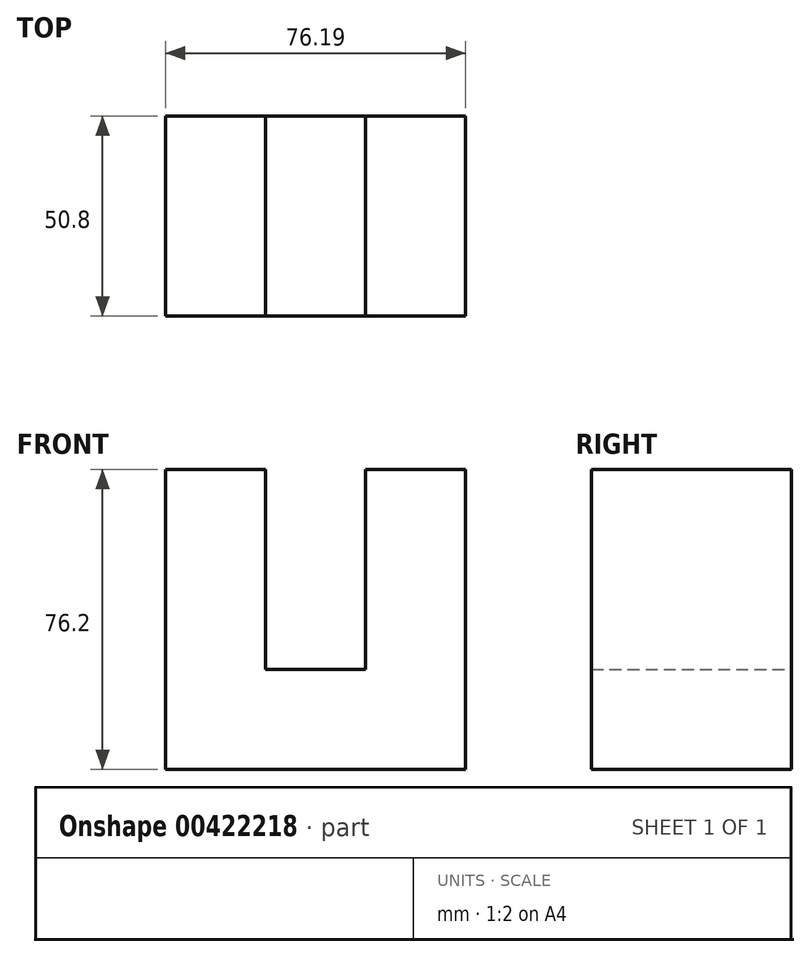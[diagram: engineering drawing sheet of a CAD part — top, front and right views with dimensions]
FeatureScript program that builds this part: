
annotation { "Feature Type Name" : "Feature", "Feature Type Description" : "" }
export const myFeature = defineFeature(function(context is Context, id is Id, definition is map)
    precondition{}
    {
        {
            var Q0;
            Q0=qCreatedBy(makeId("Front.planeOp"),FACE);
            var sketch = newSketch(context, id + "F0", { "sketchPlane" : qUnion([Q0])});
            skLineSegment(sketch, "E0", {"start": v(0, 0) * mm, "end": v(-76.2, 0) * mm});
            skLineSegment(sketch, "E1", {"start": v(-76.2, 0) * mm, "end": v(-76.2, 76.2) * mm});
            skLineSegment(sketch, "E2", {"start": v(-76.2, 76.2) * mm, "end": v(-50.8, 76.2) * mm});
            skLineSegment(sketch, "E3", {"start": v(-50.8, 76.2) * mm, "end": v(-50.8, 25.4) * mm});
            skLineSegment(sketch, "E4", {"start": v(-50.8, 25.4) * mm, "end": v(-25.4, 25.4) * mm});
            skLineSegment(sketch, "E5", {"start": v(-25.4, 25.4) * mm, "end": v(-25.4, 76.2) * mm});
            skLineSegment(sketch, "E6", {"start": v(-25.4, 76.2) * mm, "end": v(0, 76.2) * mm});
            skLineSegment(sketch, "E7", {"start": v(0, 0) * mm, "end": v(0, 76.2) * mm});
            skSolve(sketch);
        }
        {
            var Q0;
            Q0 = qSketchRegion(id + "F0", true);
            extrude(context, id + "F1", {"entities" : qUnion([Q0]), "depth" : 50.8 * mm});
        }
    });
